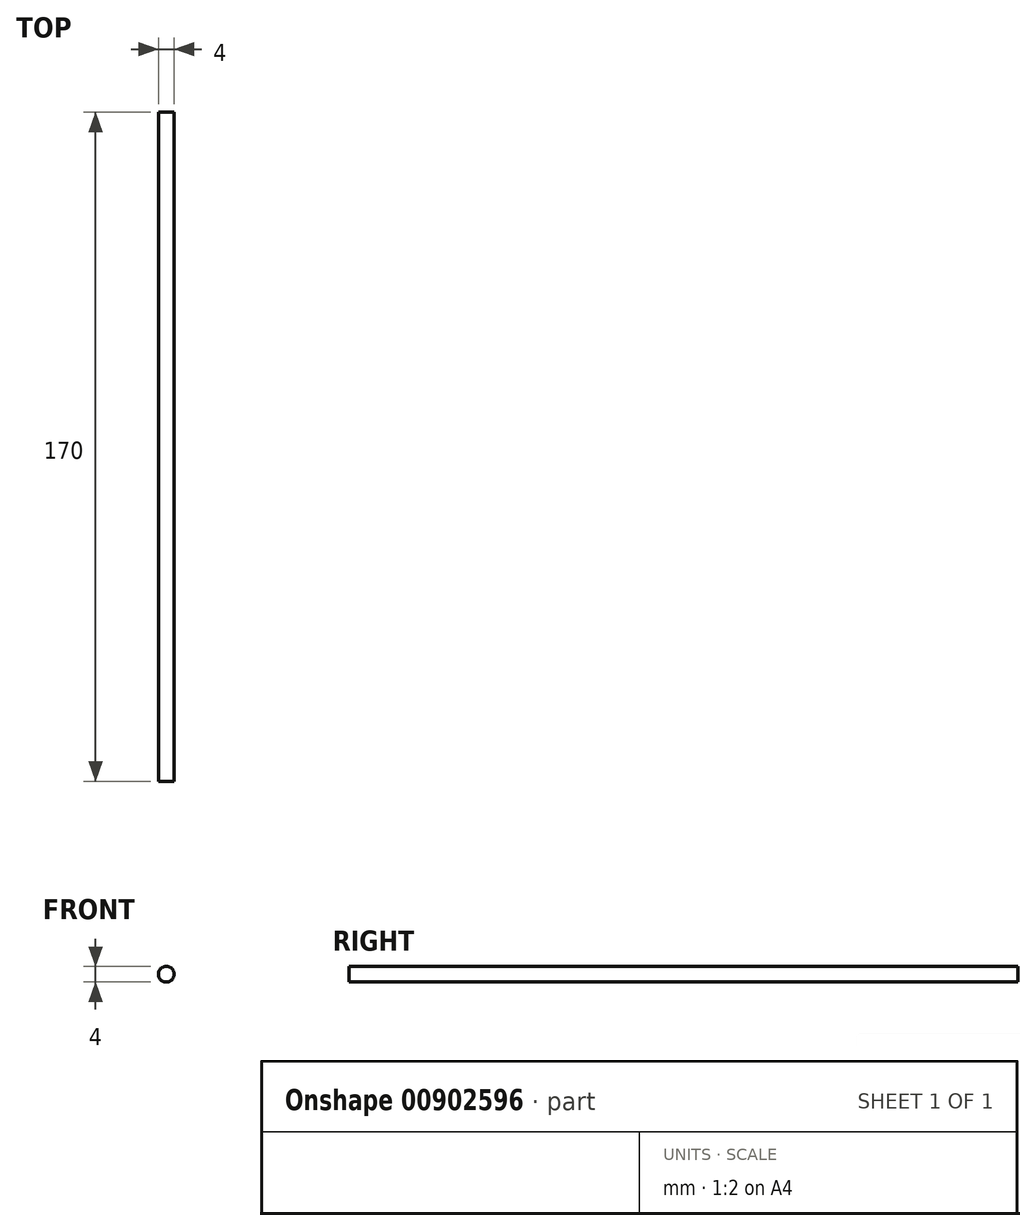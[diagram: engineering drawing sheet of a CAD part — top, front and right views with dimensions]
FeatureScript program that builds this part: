
annotation { "Feature Type Name" : "Feature", "Feature Type Description" : "" }
export const myFeature = defineFeature(function(context is Context, id is Id, definition is map)
    precondition{}
    {
        {
            var Q0;
            Q0=qCreatedBy(makeId("Front.planeOp"),FACE);
            var sketch = newSketch(context, id + "F0", { "sketchPlane" : qUnion([Q0])});
            skCircle(sketch, "E0", {"center": v(0, 0) * mm, "radius": 2 * mm});
            skSolve(sketch);
        }
        {
            var Q0;
            Q0 = qSketchRegion(id + "F0", true);
            extrude(context, id + "F1", {"entities" : qUnion([Q0]), "endBound" : BoundingType.SYMMETRIC, "depth" : 170 * mm, "offsetDistance" : 25 * mm});
        }
    });
